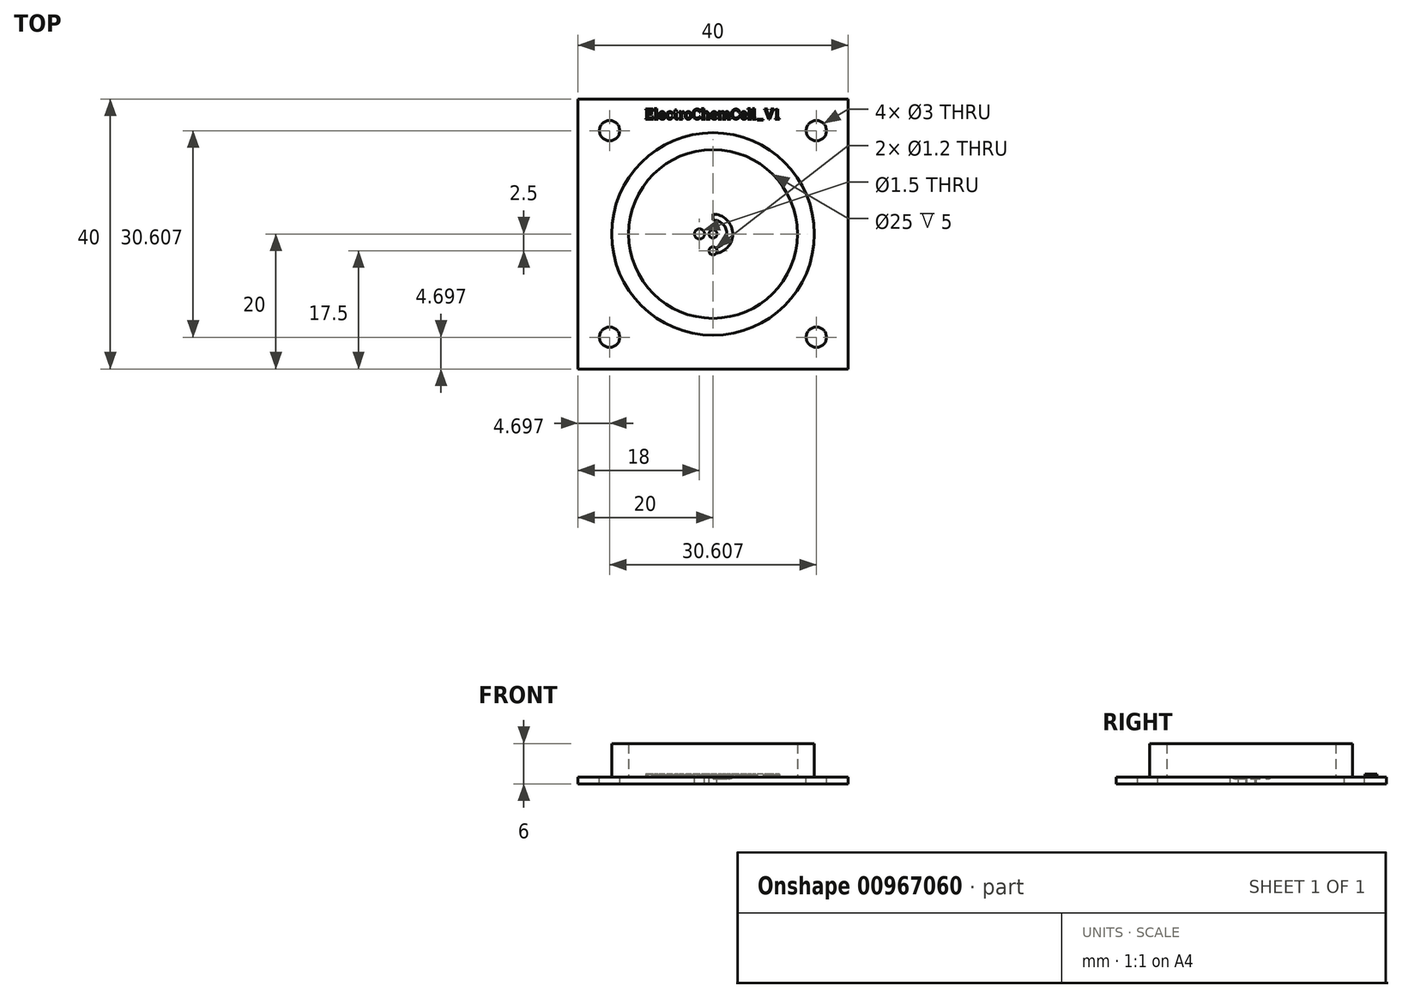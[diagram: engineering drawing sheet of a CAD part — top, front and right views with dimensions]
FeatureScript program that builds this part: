
annotation { "Feature Type Name" : "Feature", "Feature Type Description" : "" }
export const myFeature = defineFeature(function(context is Context, id is Id, definition is map)
    precondition{}
    {
        {
            var Q0;
            Q0=qCreatedBy(makeId("Top.planeOp"),FACE);
            var sketch = newSketch(context, id + "F0", { "sketchPlane" : qUnion([Q0])});
            skCircle(sketch, "E0", {"center": v(0, 0) * mm, "radius": 15 * mm});
            skLineSegment(sketch, "E1.bottom", {"start": v(20, -20) * mm, "end": v(-20, -20) * mm});
            skLineSegment(sketch, "E1.top", {"start": v(20, 20) * mm, "end": v(-20, 20) * mm});
            skLineSegment(sketch, "E1.left", {"start": v(20, -20) * mm, "end": v(20, 20) * mm});
            skLineSegment(sketch, "E1.right", {"start": v(-20, -20) * mm, "end": v(-20, 20) * mm});
            skCircle(sketch, "E2", {"center": v(0, 0) * mm, "radius": 0.6 * mm});
            skText(sketch, "E3", { "text": "ElectroChemCell_V1", "fontName": "RobotoSlab-Regular.ttf"});
            skCircle(sketch, "E4", {"center": v(0, 0) * mm, "radius": 12.5 * mm});
            skCircle(sketch, "E5", {"center": v(-2, 0) * mm, "radius": 0.75 * mm});
            skCircle(sketch, "E6", {"center": v(0, 0) * mm, "radius": 2 * mm, "construction": true});
            skCircle(sketch, "E7", {"center": v(0, 0) * mm, "radius": 3 * mm, "construction": true});
            skLineSegment(sketch, "E8", {"start": v(0, 0) * mm, "end": v(0, -3) * mm, "construction": true});
            skPoint(sketch, "E9", {"position": v(0, -2.5) * mm});
            skLineSegment(sketch, "E10", {"start": v(0, 3) * mm, "end": v(0, 2) * mm});
            skArc(sketch, "E11", {"start": v(0, 2) * mm, "mid": v(2, 0) * mm, "end": v(0, -2) * mm});
            skArc(sketch, "E12", {"start": v(0, 3) * mm, "mid": v(3, 0) * mm, "end": v(0, -3) * mm});
            skCircle(sketch, "E13", {"center": v(0, -2.5) * mm, "radius": 0.6 * mm});
            skLineSegment(sketch, "E14", {"start": v(0, 0) * mm, "end": v(-20, -20) * mm, "construction": true});
            skLineSegment(sketch, "E15", {"start": v(0, 0) * mm, "end": v(20, -20) * mm, "construction": true});
            skLineSegment(sketch, "E16", {"start": v(-10.6, -10.6) * mm, "end": v(-10.6, -20) * mm, "construction": true});
            skLineSegment(sketch, "E17", {"start": v(-10.6, -20) * mm, "end": v(-15.3, -15.3) * mm, "construction": true});
            skCircle(sketch, "E18", {"center": v(-15.3, -15.3) * mm, "radius": 1.5 * mm});
            skLineSegment(sketch, "E19", {"start": v(0, 0) * mm, "end": v(20, 20) * mm, "construction": true});
            skLineSegment(sketch, "E20", {"start": v(10.6, -10.6) * mm, "end": v(20, -10.6) * mm, "construction": true});
            skLineSegment(sketch, "E21", {"start": v(20, -10.6) * mm, "end": v(15.3, -15.3) * mm, "construction": true});
            skCircle(sketch, "E22", {"center": v(15.3, -15.3) * mm, "radius": 1.5 * mm});
            skLineSegment(sketch, "E23", {"start": v(10.6, 10.6) * mm, "end": v(20, 10.6) * mm, "construction": true});
            skLineSegment(sketch, "E24", {"start": v(20, 10.6) * mm, "end": v(15.3, 15.3) * mm, "construction": true});
            skCircle(sketch, "E25", {"center": v(15.3, 15.3) * mm, "radius": 1.5 * mm});
            skLineSegment(sketch, "E26", {"start": v(-15.3, -15.3) * mm, "end": v(-15.3, 20) * mm, "construction": true});
            skCircle(sketch, "E27", {"center": v(-15.3, 15.3) * mm, "radius": 1.5 * mm});
            skLineSegment(sketch, "E28", {"start": v(15.3, 15.3) * mm, "end": v(-20, 15.3) * mm, "construction": true});
            const initialGuessF0  = {"E3": [-0.01006, 0.01702, 1, 0, 0.00149]};
            skSetInitialGuess(sketch, initialGuessF0);
            skSolve(sketch);
        }
        {
            var Q0;
            Q0=makeQuery(id+"F0.imprint","IMPRINT",FACE,{"disambiguationData":[TD([[makeQuery(id+"F0.imprint","IMPRINT",EDGE,{"derivedFrom":sQuery(id+"F0.wireOp",EDGE,"E0")}),-1.0]])]});
            var Q1;
            Q1=makeQuery(id+"F0.imprint","IMPRINT",FACE,{"disambiguationData":[TD([[makeQuery(id+"F0.imprint","IMPRINT",EDGE,{"derivedFrom":sQuery(id+"F0.wireOp",EDGE,"E0")}),1.0]])]});
            var Q2;
            Q2=makeQuery(id+"F0.imprint","IMPRINT",FACE,{"disambiguationData":[TD([[makeQuery(id+"F0.imprint","IMPRINT",EDGE,{"derivedFrom":sQuery(id+"F0.wireOp",EDGE,"E2")}),-1.0]])]});
            var Q3;
            Q3=makeQuery(id+"F0.imprint","IMPRINT",FACE,{"disambiguationData":[TD([[makeQuery(id+"F0.imprint","IMPRINT",EDGE,{"derivedFrom":sQuery(id+"F0.wireOp",EDGE,"E10")}),1.0]])]});
            var Q4;
            Q4=makeQuery(id+"F0.imprint","IMPRINT",FACE,{"disambiguationData":[TD([[makeQuery(id+"F0.imprint","IMPRINT",EDGE,{"derivedFrom":sQuery(id+"F0.wireOp",EDGE,"E3.sketch_text.stroke-0")}),-1.0]])]});
            var Q5;
            Q5=makeQuery(id+"F0.imprint","IMPRINT",FACE,{"disambiguationData":[TD([[makeQuery(id+"F0.imprint","IMPRINT",EDGE,{"derivedFrom":sQuery(id+"F0.wireOp",EDGE,"E3.sketch_text.stroke-20")}),-1.0]])]});
            var Q6;
            Q6=makeQuery(id+"F0.imprint","IMPRINT",FACE,{"disambiguationData":[TD([[makeQuery(id+"F0.imprint","IMPRINT",EDGE,{"derivedFrom":sQuery(id+"F0.wireOp",EDGE,"E3.sketch_text.stroke-30")}),-1.0]])]});
            var Q7;
            Q7=makeQuery(id+"F0.imprint","IMPRINT",FACE,{"disambiguationData":[TD([[makeQuery(id+"F0.imprint","IMPRINT",EDGE,{"derivedFrom":sQuery(id+"F0.wireOp",EDGE,"E3.sketch_text.stroke-47")}),1.0]])]});
            var Q8;
            Q8=makeQuery(id+"F0.imprint","IMPRINT",FACE,{"disambiguationData":[TD([[makeQuery(id+"F0.imprint","IMPRINT",EDGE,{"derivedFrom":sQuery(id+"F0.wireOp",EDGE,"E3.sketch_text.stroke-54")}),-1.0]])]});
            var Q9;
            Q9=makeQuery(id+"F0.imprint","IMPRINT",FACE,{"disambiguationData":[TD([[makeQuery(id+"F0.imprint","IMPRINT",EDGE,{"derivedFrom":sQuery(id+"F0.wireOp",EDGE,"E3.sketch_text.stroke-77")}),-1.0]])]});
            var Q10;
            Q10=makeQuery(id+"F0.imprint","IMPRINT",FACE,{"disambiguationData":[TD([[makeQuery(id+"F0.imprint","IMPRINT",EDGE,{"derivedFrom":sQuery(id+"F0.wireOp",EDGE,"E3.sketch_text.stroke-97")}),-1.0]])]});
            var Q11;
            Q11=makeQuery(id+"F0.imprint","IMPRINT",FACE,{"disambiguationData":[TD([[makeQuery(id+"F0.imprint","IMPRINT",EDGE,{"derivedFrom":sQuery(id+"F0.wireOp",EDGE,"E3.sketch_text.stroke-126")}),1.0]])]});
            var Q12;
            Q12=makeQuery(id+"F0.imprint","IMPRINT",FACE,{"disambiguationData":[TD([[makeQuery(id+"F0.imprint","IMPRINT",EDGE,{"derivedFrom":sQuery(id+"F0.wireOp",EDGE,"E3.sketch_text.stroke-116")}),-1.0]])]});
            var Q13;
            Q13=makeQuery(id+"F0.imprint","IMPRINT",FACE,{"disambiguationData":[TD([[makeQuery(id+"F0.imprint","IMPRINT",EDGE,{"derivedFrom":sQuery(id+"F0.wireOp",EDGE,"E3.sketch_text.stroke-136")}),-1.0]])]});
            var Q14;
            Q14=makeQuery(id+"F0.imprint","IMPRINT",FACE,{"disambiguationData":[TD([[makeQuery(id+"F0.imprint","IMPRINT",EDGE,{"derivedFrom":sQuery(id+"F0.wireOp",EDGE,"E3.sketch_text.stroke-160")}),-1.0]])]});
            var Q15;
            Q15=makeQuery(id+"F0.imprint","IMPRINT",FACE,{"disambiguationData":[TD([[makeQuery(id+"F0.imprint","IMPRINT",EDGE,{"derivedFrom":sQuery(id+"F0.wireOp",EDGE,"E3.sketch_text.stroke-203")}),1.0]])]});
            var Q16;
            Q16=makeQuery(id+"F0.imprint","IMPRINT",FACE,{"disambiguationData":[TD([[makeQuery(id+"F0.imprint","IMPRINT",EDGE,{"derivedFrom":sQuery(id+"F0.wireOp",EDGE,"E3.sketch_text.stroke-186")}),-1.0]])]});
            var Q17;
            Q17=makeQuery(id+"F0.imprint","IMPRINT",FACE,{"disambiguationData":[TD([[makeQuery(id+"F0.imprint","IMPRINT",EDGE,{"derivedFrom":sQuery(id+"F0.wireOp",EDGE,"E3.sketch_text.stroke-210")}),-1.0]])]});
            var Q18;
            Q18=makeQuery(id+"F0.imprint","IMPRINT",FACE,{"disambiguationData":[TD([[makeQuery(id+"F0.imprint","IMPRINT",EDGE,{"derivedFrom":sQuery(id+"F0.wireOp",EDGE,"E3.sketch_text.stroke-251")}),-1.0]])]});
            var Q19;
            Q19=makeQuery(id+"F0.imprint","IMPRINT",FACE,{"disambiguationData":[TD([[makeQuery(id+"F0.imprint","IMPRINT",EDGE,{"derivedFrom":sQuery(id+"F0.wireOp",EDGE,"E3.sketch_text.stroke-292")}),1.0]])]});
            var Q20;
            Q20=makeQuery(id+"F0.imprint","IMPRINT",FACE,{"disambiguationData":[TD([[makeQuery(id+"F0.imprint","IMPRINT",EDGE,{"derivedFrom":sQuery(id+"F0.wireOp",EDGE,"E3.sketch_text.stroke-275")}),-1.0]])]});
            var Q21;
            Q21=makeQuery(id+"F0.imprint","IMPRINT",FACE,{"disambiguationData":[TD([[makeQuery(id+"F0.imprint","IMPRINT",EDGE,{"derivedFrom":sQuery(id+"F0.wireOp",EDGE,"E3.sketch_text.stroke-299")}),-1.0]])]});
            var Q22;
            Q22=makeQuery(id+"F0.imprint","IMPRINT",FACE,{"disambiguationData":[TD([[makeQuery(id+"F0.imprint","IMPRINT",EDGE,{"derivedFrom":sQuery(id+"F0.wireOp",EDGE,"E3.sketch_text.stroke-309")}),-1.0]])]});
            var Q23;
            Q23=makeQuery(id+"F0.imprint","IMPRINT",FACE,{"disambiguationData":[TD([[makeQuery(id+"F0.imprint","IMPRINT",EDGE,{"derivedFrom":sQuery(id+"F0.wireOp",EDGE,"E3.sketch_text.stroke-319")}),-1.0]])]});
            var Q24;
            Q24=makeQuery(id+"F0.imprint","IMPRINT",FACE,{"disambiguationData":[TD([[makeQuery(id+"F0.imprint","IMPRINT",EDGE,{"derivedFrom":sQuery(id+"F0.wireOp",EDGE,"E3.sketch_text.stroke-323")}),-1.0]])]});
            var Q25;
            Q25=makeQuery(id+"F0.imprint","IMPRINT",FACE,{"disambiguationData":[TD([[makeQuery(id+"F0.imprint","IMPRINT",EDGE,{"derivedFrom":sQuery(id+"F0.wireOp",EDGE,"E3.sketch_text.stroke-341")}),-1.0]])]});
            extrude(context, id + "F1", {"entities" : qUnion([Q0, Q1, Q2, Q3, Q4, Q5, Q6, Q7, Q8, Q9, Q10, Q11, Q12, Q13, Q14, Q15, Q16, Q17, Q18, Q19, Q20, Q21, Q22, Q23, Q24, Q25]), "oppositeDirection" : true, "depth" : 1 * mm, "offsetDistance" : 25 * mm});
        }
        {
            var Q0;
            Q0=makeQuery(id+"F0.imprint","IMPRINT",FACE,{"disambiguationData":[TD([[makeQuery(id+"F0.imprint","IMPRINT",EDGE,{"derivedFrom":sQuery(id+"F0.wireOp",EDGE,"E0")}),1.0]])]});
            extrude(context, id + "F2", {"entities" : qUnion([Q0]), "operationType" : NewBodyOperationType.ADD, "depth" : 5 * mm, "offsetDistance" : 25 * mm});
        }
        {
            var Q0;
            Q0=makeQuery(id+"F0.imprint","IMPRINT",FACE,{"disambiguationData":[TD([[makeQuery(id+"F0.imprint","IMPRINT",EDGE,{"derivedFrom":sQuery(id+"F0.wireOp",EDGE,"E3.sketch_text.stroke-0")}),-1.0]])]});
            var Q1;
            Q1=makeQuery(id+"F0.imprint","IMPRINT",FACE,{"disambiguationData":[TD([[makeQuery(id+"F0.imprint","IMPRINT",EDGE,{"derivedFrom":sQuery(id+"F0.wireOp",EDGE,"E3.sketch_text.stroke-20")}),-1.0]])]});
            var Q2;
            Q2=makeQuery(id+"F0.imprint","IMPRINT",FACE,{"disambiguationData":[TD([[makeQuery(id+"F0.imprint","IMPRINT",EDGE,{"derivedFrom":sQuery(id+"F0.wireOp",EDGE,"E3.sketch_text.stroke-30")}),-1.0]])]});
            var Q3;
            Q3=makeQuery(id+"F0.imprint","IMPRINT",FACE,{"disambiguationData":[TD([[makeQuery(id+"F0.imprint","IMPRINT",EDGE,{"derivedFrom":sQuery(id+"F0.wireOp",EDGE,"E3.sketch_text.stroke-54")}),-1.0]])]});
            var Q4;
            Q4=makeQuery(id+"F0.imprint","IMPRINT",FACE,{"disambiguationData":[TD([[makeQuery(id+"F0.imprint","IMPRINT",EDGE,{"derivedFrom":sQuery(id+"F0.wireOp",EDGE,"E3.sketch_text.stroke-77")}),-1.0]])]});
            var Q5;
            Q5=makeQuery(id+"F0.imprint","IMPRINT",FACE,{"disambiguationData":[TD([[makeQuery(id+"F0.imprint","IMPRINT",EDGE,{"derivedFrom":sQuery(id+"F0.wireOp",EDGE,"E3.sketch_text.stroke-97")}),-1.0]])]});
            var Q6;
            Q6=makeQuery(id+"F0.imprint","IMPRINT",FACE,{"disambiguationData":[TD([[makeQuery(id+"F0.imprint","IMPRINT",EDGE,{"derivedFrom":sQuery(id+"F0.wireOp",EDGE,"E3.sketch_text.stroke-116")}),-1.0]])]});
            var Q7;
            Q7=makeQuery(id+"F0.imprint","IMPRINT",FACE,{"disambiguationData":[TD([[makeQuery(id+"F0.imprint","IMPRINT",EDGE,{"derivedFrom":sQuery(id+"F0.wireOp",EDGE,"E3.sketch_text.stroke-136")}),-1.0]])]});
            var Q8;
            Q8=makeQuery(id+"F0.imprint","IMPRINT",FACE,{"disambiguationData":[TD([[makeQuery(id+"F0.imprint","IMPRINT",EDGE,{"derivedFrom":sQuery(id+"F0.wireOp",EDGE,"E3.sketch_text.stroke-160")}),-1.0]])]});
            var Q9;
            Q9=makeQuery(id+"F0.imprint","IMPRINT",FACE,{"disambiguationData":[TD([[makeQuery(id+"F0.imprint","IMPRINT",EDGE,{"derivedFrom":sQuery(id+"F0.wireOp",EDGE,"E3.sketch_text.stroke-186")}),-1.0]])]});
            var Q10;
            Q10=makeQuery(id+"F0.imprint","IMPRINT",FACE,{"disambiguationData":[TD([[makeQuery(id+"F0.imprint","IMPRINT",EDGE,{"derivedFrom":sQuery(id+"F0.wireOp",EDGE,"E3.sketch_text.stroke-210")}),-1.0]])]});
            var Q11;
            Q11=makeQuery(id+"F0.imprint","IMPRINT",FACE,{"disambiguationData":[TD([[makeQuery(id+"F0.imprint","IMPRINT",EDGE,{"derivedFrom":sQuery(id+"F0.wireOp",EDGE,"E3.sketch_text.stroke-251")}),-1.0]])]});
            var Q12;
            Q12=makeQuery(id+"F0.imprint","IMPRINT",FACE,{"disambiguationData":[TD([[makeQuery(id+"F0.imprint","IMPRINT",EDGE,{"derivedFrom":sQuery(id+"F0.wireOp",EDGE,"E3.sketch_text.stroke-275")}),-1.0]])]});
            var Q13;
            Q13=makeQuery(id+"F0.imprint","IMPRINT",FACE,{"disambiguationData":[TD([[makeQuery(id+"F0.imprint","IMPRINT",EDGE,{"derivedFrom":sQuery(id+"F0.wireOp",EDGE,"E3.sketch_text.stroke-299")}),-1.0]])]});
            var Q14;
            Q14=makeQuery(id+"F0.imprint","IMPRINT",FACE,{"disambiguationData":[TD([[makeQuery(id+"F0.imprint","IMPRINT",EDGE,{"derivedFrom":sQuery(id+"F0.wireOp",EDGE,"E3.sketch_text.stroke-309")}),-1.0]])]});
            var Q15;
            Q15=makeQuery(id+"F0.imprint","IMPRINT",FACE,{"disambiguationData":[TD([[makeQuery(id+"F0.imprint","IMPRINT",EDGE,{"derivedFrom":sQuery(id+"F0.wireOp",EDGE,"E3.sketch_text.stroke-319")}),-1.0]])]});
            var Q16;
            Q16=makeQuery(id+"F0.imprint","IMPRINT",FACE,{"disambiguationData":[TD([[makeQuery(id+"F0.imprint","IMPRINT",EDGE,{"derivedFrom":sQuery(id+"F0.wireOp",EDGE,"E3.sketch_text.stroke-323")}),-1.0]])]});
            var Q17;
            Q17=makeQuery(id+"F0.imprint","IMPRINT",FACE,{"disambiguationData":[TD([[makeQuery(id+"F0.imprint","IMPRINT",EDGE,{"derivedFrom":sQuery(id+"F0.wireOp",EDGE,"E3.sketch_text.stroke-341")}),-1.0]])]});
            extrude(context, id + "F3", {"entities" : qUnion([Q0, Q1, Q2, Q3, Q4, Q5, Q6, Q7, Q8, Q9, Q10, Q11, Q12, Q13, Q14, Q15, Q16, Q17]), "operationType" : NewBodyOperationType.ADD, "depth" : 0.5 * mm, "offsetDistance" : 25 * mm});
        }
        {
            var Q0;
            Q0=qCreatedBy(makeId("Front.planeOp"),FACE);
            var sketch = newSketch(context, id + "F4", { "sketchPlane" : qUnion([Q0])});
            skCircle(sketch, "E29", {"center": v(2.5, 0) * mm, "radius": 0.5 * mm, "construction": true});
            skLineSegment(sketch, "E30", {"start": v(2.5, 0) * mm, "end": v(2.5, 0.5) * mm, "construction": true});
            skPoint(sketch, "E31", {"position": v(2.5, 0.25) * mm});
            skCircle(sketch, "E32", {"center": v(2.5, 0.25) * mm, "radius": 0.5 * mm});
            skSolve(sketch);
        }
        {
            var Q0;
            Q0=makeQuery(id+"F4.imprint","IMPRINT",FACE,{"disambiguationData":[TD([[makeQuery(id+"F4.imprint","IMPRINT",EDGE,{"derivedFrom":sQuery(id+"F4.wireOp",EDGE,"E32")}),1.0]])]});
            var Q1;
            Q1=sQuery(id+"F4.wireOp",EDGE,"E32");
            var Q2;
            Q2=makeQuery(id+"F1.opExtrude","SWEPT_FACE",FACE,{"disambiguationData":[OSD([sQuery(id+"F0.wireOp",EDGE,"E2")])]});
            revolve(context, id + "F5", {"operationType" : NewBodyOperationType.REMOVE, "surfaceOperationType" : NewSurfaceOperationType.NEW, "entities" : qUnion([Q0]), "surfaceEntities" : qUnion([Q1]), "axis" : qUnion([Q2]), "revolveType" : RevolveType.SYMMETRIC, "angle" : 180 * degree});
        }
    });
